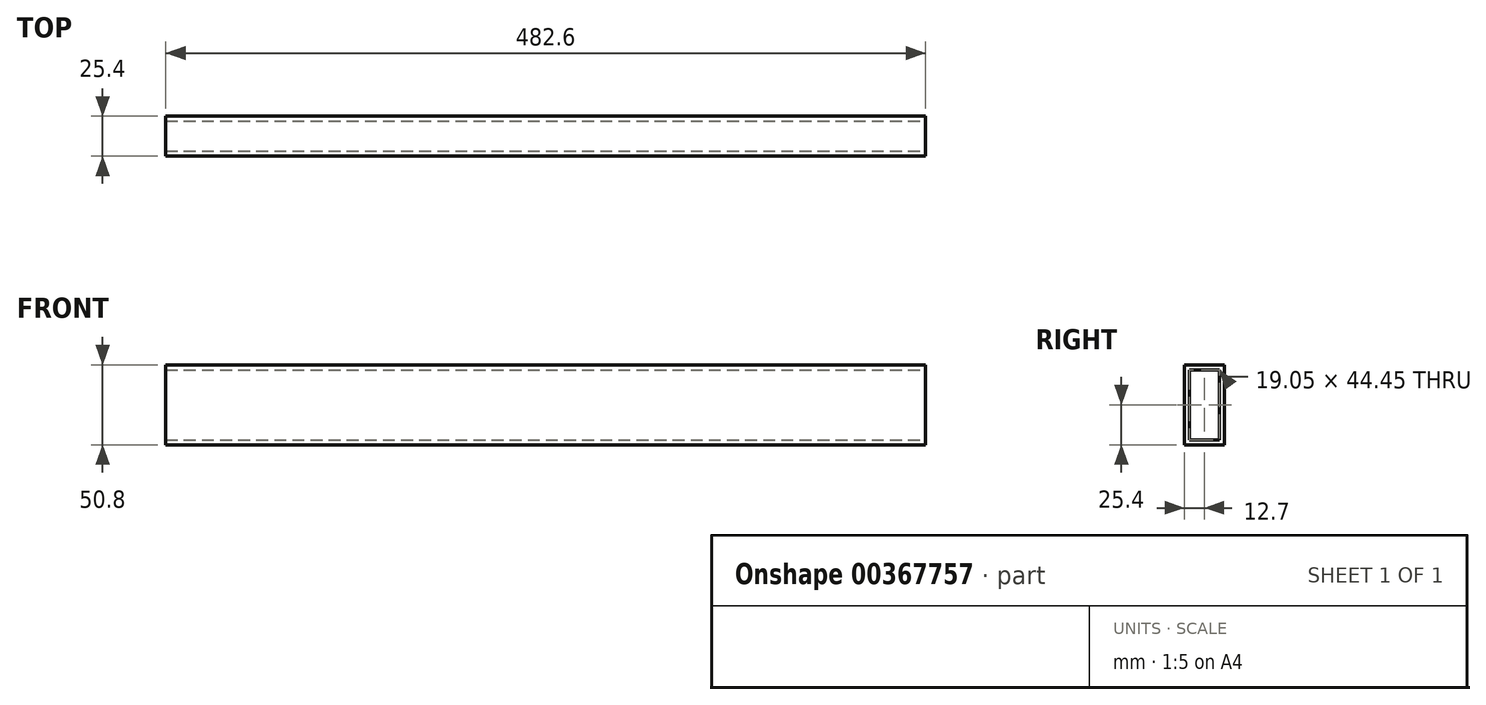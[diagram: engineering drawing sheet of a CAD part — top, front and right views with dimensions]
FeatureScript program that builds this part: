
annotation { "Feature Type Name" : "Feature", "Feature Type Description" : "" }
export const myFeature = defineFeature(function(context is Context, id is Id, definition is map)
    precondition{}
    {
        {
            var Q0;
            Q0=qCreatedBy(makeId("Front.planeOp"),FACE);
            var sketch = newSketch(context, id + "F0", { "sketchPlane" : qUnion([Q0])});
            skLineSegment(sketch, "E0.bottom", {"start": v(-241.3, 0) * mm, "end": v(241.3, 0) * mm});
            skLineSegment(sketch, "E0.top", {"start": v(-241.3, -50.8) * mm, "end": v(241.3, -50.8) * mm});
            skLineSegment(sketch, "E0.left", {"start": v(-241.3, 0) * mm, "end": v(-241.3, -50.8) * mm});
            skLineSegment(sketch, "E0.right", {"start": v(241.3, 0) * mm, "end": v(241.3, -50.8) * mm});
            skSolve(sketch);
        }
        {
            var Q0;
            Q0 = qSketchRegion(id + "F0", true);
            extrude(context, id + "F1", {"entities" : qUnion([Q0]), "depth" : 25.4 * mm});
        }
        {
            var Q0;
            Q0=makeQuery(id+"F1.opExtrude","SWEPT_FACE",FACE,{"disambiguationData":[OSD([sQuery(id+"F0.wireOp",EDGE,"E0.right")])]});
            var sketch = newSketch(context, id + "F2", { "sketchPlane" : qUnion([Q0])});
            skLineSegment(sketch, "E1.bottom", {"start": v(-22.23, -3.18) * mm, "end": v(-3.18, -3.18) * mm});
            skLineSegment(sketch, "E1.top", {"start": v(-22.23, -47.62) * mm, "end": v(-3.17, -47.62) * mm});
            skLineSegment(sketch, "E1.left", {"start": v(-22.23, -3.18) * mm, "end": v(-22.23, -47.62) * mm});
            skLineSegment(sketch, "E1.right", {"start": v(-3.18, -3.18) * mm, "end": v(-3.18, -47.62) * mm});
            skSolve(sketch);
        }
        {
            var Q0;
            Q0=makeQuery(id+"F2.imprint","IMPRINT",FACE,{"disambiguationData":[TD([[makeQuery(id+"F2.imprint","IMPRINT",EDGE,{"derivedFrom":sQuery(id+"F2.wireOp",EDGE,"E1.bottom")}),-1.0]])]});
            extrude(context, id + "F3", {"entities" : qUnion([Q0]), "operationType" : NewBodyOperationType.REMOVE, "oppositeDirection" : true, "depth" : 482.6 * mm});
        }
    });
